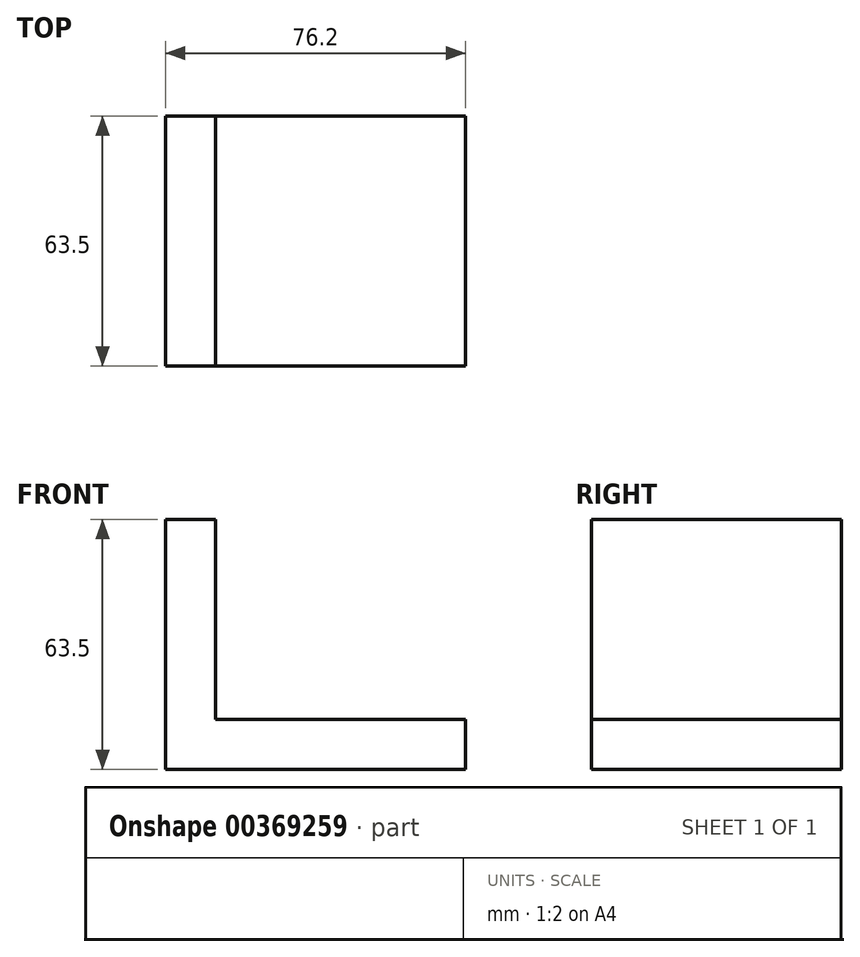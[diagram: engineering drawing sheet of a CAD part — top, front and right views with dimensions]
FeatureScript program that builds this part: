
annotation { "Feature Type Name" : "Feature", "Feature Type Description" : "" }
export const myFeature = defineFeature(function(context is Context, id is Id, definition is map)
    precondition{}
    {
        {
            var Q0;
            Q0=qCreatedBy(makeId("Front.planeOp"),FACE);
            var sketch = newSketch(context, id + "F0", { "sketchPlane" : qUnion([Q0])});
            skLineSegment(sketch, "E0.bottom", {"start": v(0, 0) * mm, "end": v(12.7, 0) * mm});
            skLineSegment(sketch, "E0.top", {"start": v(0, -63.5) * mm, "end": v(12.7, -63.5) * mm});
            skLineSegment(sketch, "E0.left", {"start": v(0, 0) * mm, "end": v(0, -63.5) * mm});
            skLineSegment(sketch, "E0.right", {"start": v(12.7, 0) * mm, "end": v(12.7, -63.5) * mm});
            skLineSegment(sketch, "E1.bottom", {"start": v(12.7, -63.5) * mm, "end": v(63.5, -63.5) * mm});
            skLineSegment(sketch, "E1.top", {"start": v(12.7, -50.8) * mm, "end": v(63.5, -50.8) * mm});
            skLineSegment(sketch, "E1.left", {"start": v(12.7, -63.5) * mm, "end": v(12.7, -50.8) * mm});
            skLineSegment(sketch, "E1.right", {"start": v(63.5, -63.5) * mm, "end": v(63.5, -50.8) * mm});
            skLineSegment(sketch, "E2.bottom", {"start": v(63.5, -50.8) * mm, "end": v(76.2, -50.8) * mm});
            skLineSegment(sketch, "E2.top", {"start": v(63.5, -63.5) * mm, "end": v(76.2, -63.5) * mm});
            skLineSegment(sketch, "E2.left", {"start": v(63.5, -50.8) * mm, "end": v(63.5, -63.5) * mm});
            skLineSegment(sketch, "E2.right", {"start": v(76.2, -50.8) * mm, "end": v(76.2, -63.5) * mm});
            skSolve(sketch);
        }
        {
            var Q0;
            Q0=makeQuery(id+"F0.imprint","IMPRINT",FACE,{"disambiguationData":[TD([[makeQuery(id+"F0.imprint","IMPRINT",EDGE,{"derivedFrom":sQuery(id+"F0.wireOp",EDGE,"E2.bottom")}),-1.0]])]});
            var Q1;
            Q1=makeQuery(id+"F0.imprint","IMPRINT",FACE,{"disambiguationData":[TD([[makeQuery(id+"F0.imprint","IMPRINT",EDGE,{"derivedFrom":sQuery(id+"F0.wireOp",EDGE,"E1.bottom")}),1.0]])]});
            var Q2;
            Q2=makeQuery(id+"F0.imprint","IMPRINT",FACE,{"disambiguationData":[TD([[makeQuery(id+"F0.imprint","IMPRINT",EDGE,{"derivedFrom":sQuery(id+"F0.wireOp",EDGE,"E0.bottom")}),-1.0]])]});
            extrude(context, id + "F1", {"entities" : qUnion([Q0, Q1, Q2]), "oppositeDirection" : true, "depth" : 63.5 * mm});
        }
    });
